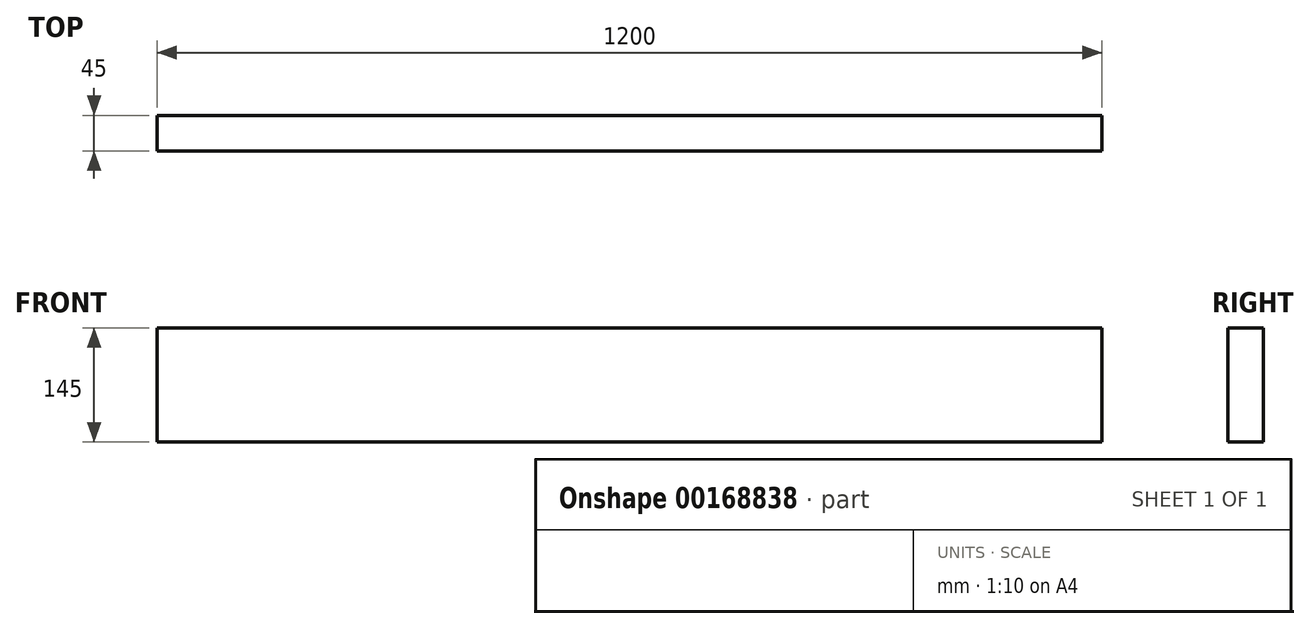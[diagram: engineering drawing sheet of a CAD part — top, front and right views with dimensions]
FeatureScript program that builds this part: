
annotation { "Feature Type Name" : "Feature", "Feature Type Description" : "" }
export const myFeature = defineFeature(function(context is Context, id is Id, definition is map)
    precondition{}
    {
        {
            var Q0;
            Q0=qCreatedBy(makeId("Right.planeOp"),FACE);
            var sketch = newSketch(context, id + "F0", { "sketchPlane" : qUnion([Q0])});
            skLineSegment(sketch, "E0.bottom", {"start": v(-22.5, 0) * mm, "end": v(22.5, 0) * mm});
            skLineSegment(sketch, "E0.top", {"start": v(-22.5, 145) * mm, "end": v(22.5, 145) * mm});
            skLineSegment(sketch, "E0.left", {"start": v(-22.5, 0) * mm, "end": v(-22.5, 145) * mm});
            skLineSegment(sketch, "E0.right", {"start": v(22.5, 0) * mm, "end": v(22.5, 145) * mm});
            skSolve(sketch);
        }
        {
            var Q0;
            Q0=makeQuery(id+"F0.imprint","IMPRINT",FACE,{"disambiguationData":[TD([[makeQuery(id+"F0.imprint","IMPRINT",EDGE,{"derivedFrom":sQuery(id+"F0.wireOp",EDGE,"E0.bottom")}),1.0]])]});
            extrude(context, id + "F1", {"entities" : qUnion([Q0]), "oppositeDirection" : true, "depth" : 1200 * mm});
        }
    });
